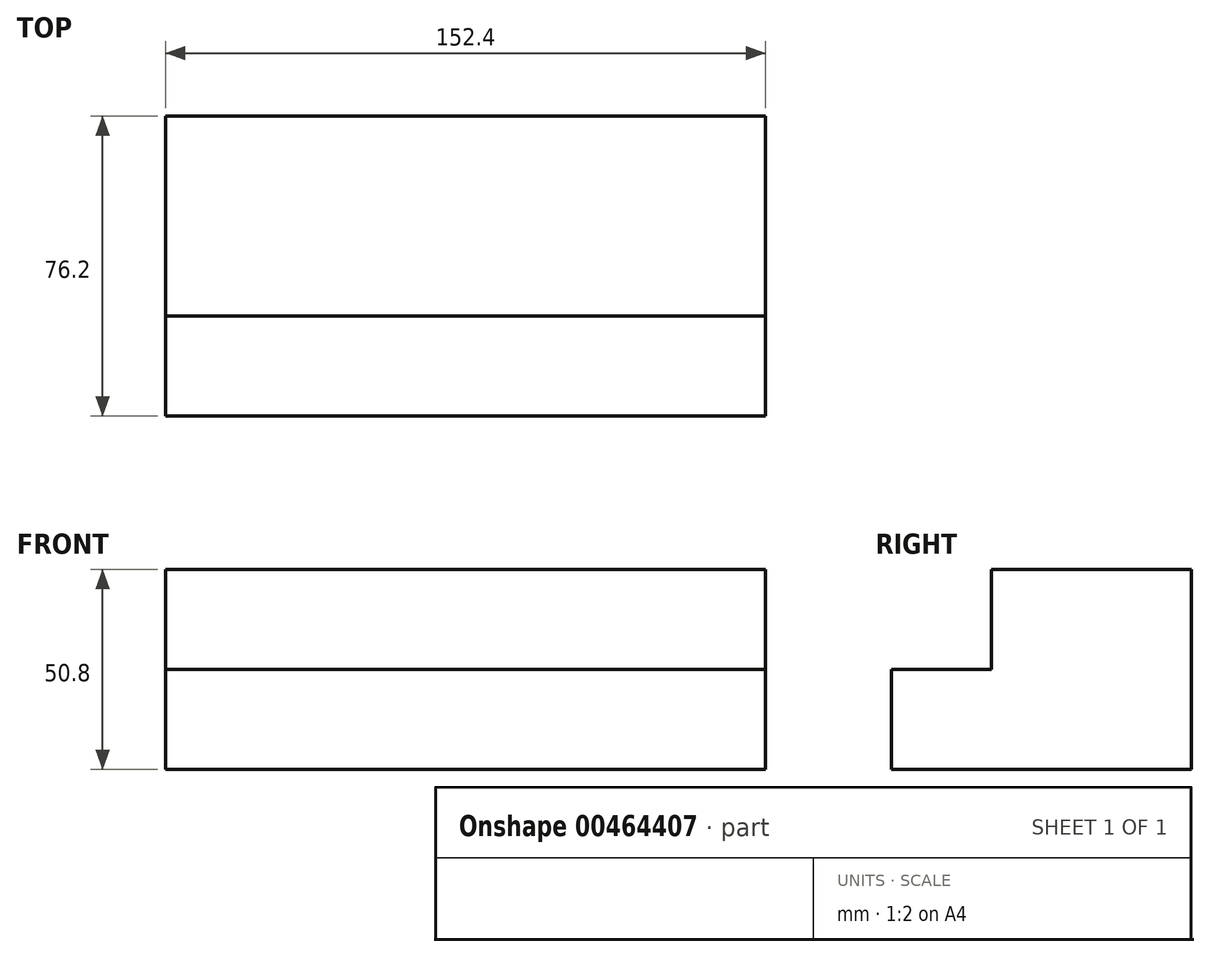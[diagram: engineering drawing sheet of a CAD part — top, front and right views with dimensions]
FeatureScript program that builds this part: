
annotation { "Feature Type Name" : "Feature", "Feature Type Description" : "" }
export const myFeature = defineFeature(function(context is Context, id is Id, definition is map)
    precondition{}
    {
        {
            var Q0;
            Q0=qCreatedBy(makeId("Right.planeOp"),FACE);
            var sketch = newSketch(context, id + "F0", { "sketchPlane" : qUnion([Q0])});
            skLineSegment(sketch, "E0", {"start": v(62.62, 52.37) * mm, "end": v(11.82, 52.37) * mm});
            skLineSegment(sketch, "E1", {"start": v(11.82, 52.37) * mm, "end": v(11.82, 26.97) * mm});
            skLineSegment(sketch, "E2", {"start": v(11.82, 26.97) * mm, "end": v(-13.58, 26.97) * mm});
            skLineSegment(sketch, "E3", {"start": v(-13.58, 26.97) * mm, "end": v(-13.58, 1.57) * mm});
            skLineSegment(sketch, "E4", {"start": v(-13.58, 1.57) * mm, "end": v(62.62, 1.57) * mm});
            skLineSegment(sketch, "E5", {"start": v(62.62, 1.57) * mm, "end": v(62.62, 52.37) * mm});
            skSolve(sketch);
        }
        {
            var Q0;
            Q0=makeQuery(id+"F0.imprint","IMPRINT",FACE,{"disambiguationData":[TD([[makeQuery(id+"F0.imprint","IMPRINT",EDGE,{"derivedFrom":sQuery(id+"F0.wireOp",EDGE,"E0")}),1.0]])]});
            extrude(context, id + "F1", {"entities" : qUnion([Q0]), "depth" : 152.4 * mm});
        }
    });
